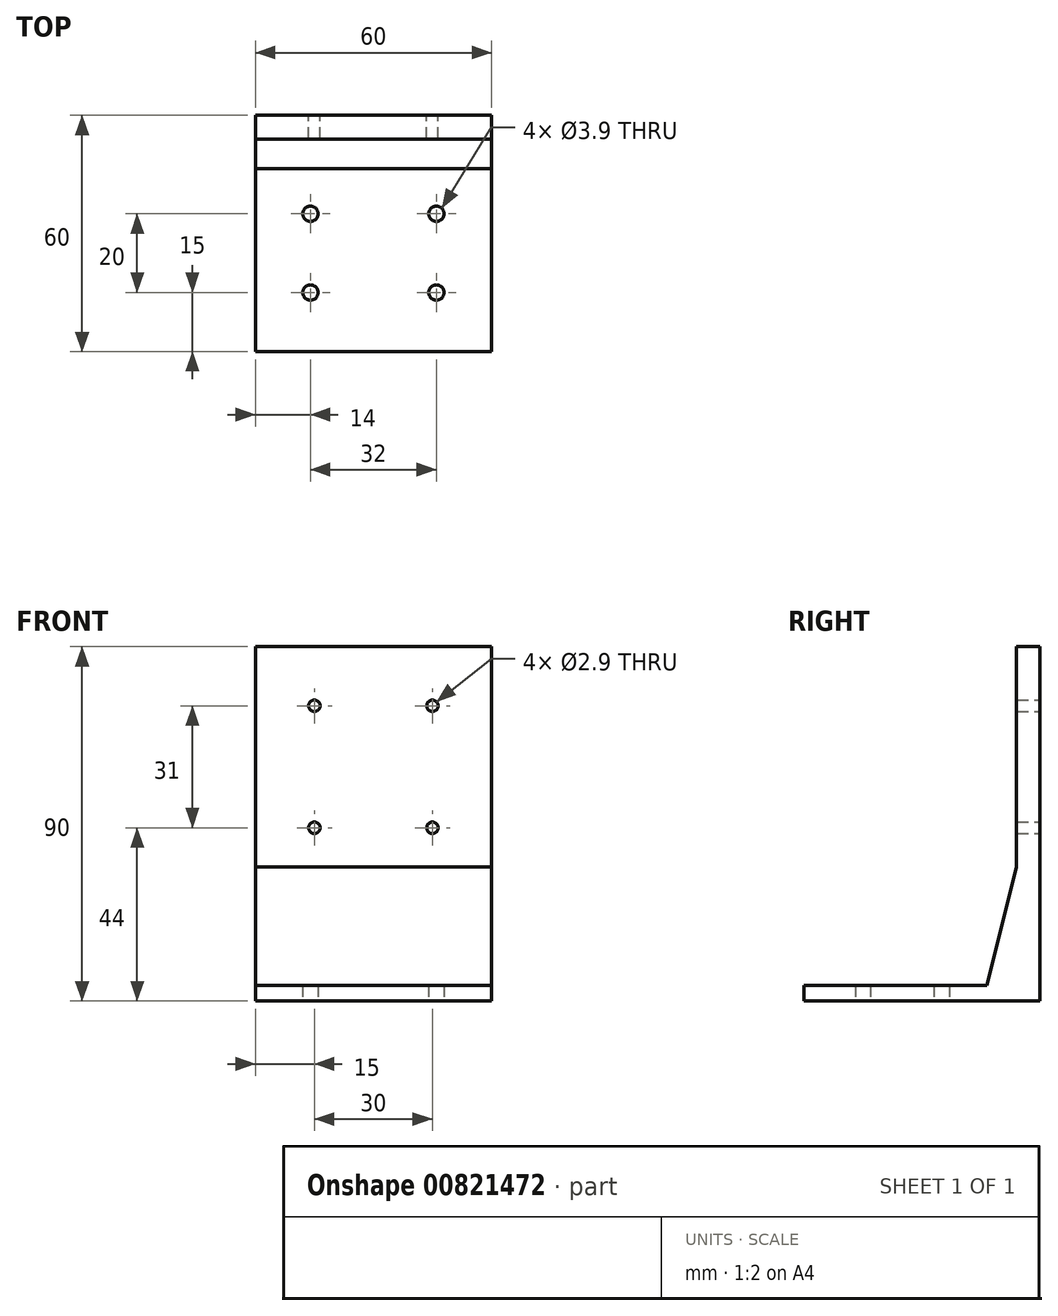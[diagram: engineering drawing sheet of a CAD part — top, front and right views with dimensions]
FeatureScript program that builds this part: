
annotation { "Feature Type Name" : "Feature", "Feature Type Description" : "" }
export const myFeature = defineFeature(function(context is Context, id is Id, definition is map)
    precondition{}
    {
        {
            var Q0;
            Q0=qCreatedBy(makeId("Top.planeOp"),FACE);
            var sketch = newSketch(context, id + "F0", { "sketchPlane" : qUnion([Q0])});
            skLineSegment(sketch, "E0.bottom", {"start": v(-30, 30) * mm, "end": v(30, 30) * mm});
            skLineSegment(sketch, "E0.top", {"start": v(-30, -30) * mm, "end": v(30, -30) * mm});
            skLineSegment(sketch, "E0.left", {"start": v(-30, 30) * mm, "end": v(-30, -30) * mm});
            skLineSegment(sketch, "E0.right", {"start": v(30, 30) * mm, "end": v(30, -30) * mm});
            skPoint(sketch, "E0.middle", {"position": v(0, 0) * mm});
            skCircle(sketch, "E1", {"center": v(-16, -15) * mm, "radius": 1.95 * mm});
            skCircle(sketch, "E2", {"center": v(16, -15) * mm, "radius": 1.95 * mm});
            skCircle(sketch, "E3", {"center": v(-16, 5) * mm, "radius": 1.95 * mm});
            skCircle(sketch, "E4", {"center": v(16, 5) * mm, "radius": 1.95 * mm});
            skSolve(sketch);
        }
        {
            var Q0;
            Q0=makeQuery(id+"F0.imprint","IMPRINT",FACE,{"disambiguationData":[TD([[makeQuery(id+"F0.imprint","IMPRINT",EDGE,{"derivedFrom":sQuery(id+"F0.wireOp",EDGE,"E0.bottom")}),-1.0]])]});
            extrude(context, id + "F1", {"entities" : qUnion([Q0]), "depth" : 4 * mm, "offsetDistance" : 25 * mm});
        }
        {
            var Q0;
            Q0=makeQuery(id+"F1.opExtrude","SWEPT_FACE",FACE,{"disambiguationData":[OSD([sQuery(id+"F0.wireOp",EDGE,"E0.bottom")])]});
            var sketch = newSketch(context, id + "F2", { "sketchPlane" : qUnion([Q0])});
            skLineSegment(sketch, "E5.bottom", {"start": v(-30, 0) * mm, "end": v(30, 0) * mm});
            skLineSegment(sketch, "E5.top", {"start": v(-30, 90) * mm, "end": v(30, 90) * mm});
            skLineSegment(sketch, "E5.left", {"start": v(-30, 0) * mm, "end": v(-30, 90) * mm});
            skLineSegment(sketch, "E5.right", {"start": v(30, 0) * mm, "end": v(30, 90) * mm});
            skCircle(sketch, "E6", {"center": v(-15, 75) * mm, "radius": 1.45 * mm});
            skCircle(sketch, "E7", {"center": v(15, 75) * mm, "radius": 1.45 * mm});
            skCircle(sketch, "E8", {"center": v(-15, 44) * mm, "radius": 1.45 * mm});
            skCircle(sketch, "E9", {"center": v(15, 44) * mm, "radius": 1.45 * mm});
            skSolve(sketch);
        }
        {
            var Q0;
            {var subQ2=sQuery(id+"F2.wireOp",EDGE,"E5.top");Q0=makeQuery(id+"F2.imprint","IMPRINT",FACE,{"disambiguationData":[TD([[makeQuery(id+"F2.imprint","IMPRINT",EDGE,{"derivedFrom":subQ2}),-1.0]])]});}
            extrude(context, id + "F3", {"entities" : qUnion([Q0]), "operationType" : NewBodyOperationType.ADD, "oppositeDirection" : true, "depth" : 6 * mm, "offsetDistance" : 25 * mm});
        }
        {
            var Q0;
            Q0=makeQuery(id+"F3.boolean.opBoolean","MERGE",FACE,{"derivedFrom":[makeQuery(id+"F1.opExtrude","SWEPT_FACE",FACE,{"disambiguationData":[OSD([sQuery(id+"F0.wireOp",EDGE,"E0.right")])]}),makeQuery(id+"F3.opExtrude","SWEPT_FACE",FACE,{"disambiguationData":[OSD([sQuery(id+"F2.wireOp",EDGE,"E5.left")])]})]});
            var sketch = newSketch(context, id + "F4", { "sketchPlane" : qUnion([Q0])});
            skLineSegment(sketch, "E10", {"start": v(16.5, 4) * mm, "end": v(24, 34.08) * mm});
            skSolve(sketch);
        }
        {
            var Q0;
            {var subQ0=sQuery(id+"F4.wireOp",EDGE,"E10");Q0=makeQuery(id+"F4.imprint","IMPRINT",FACE,{"disambiguationData":[TD([[makeQuery(id+"F4.imprint","IMPRINT",EDGE,{"derivedFrom":subQ0}),-1.0]])]});}
            extrude(context, id + "F5", {"entities" : qUnion([Q0]), "operationType" : NewBodyOperationType.ADD, "oppositeDirection" : true, "depth" : 60 * mm, "offsetDistance" : 25 * mm});
        }
    });
